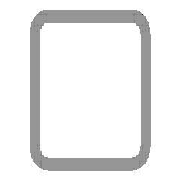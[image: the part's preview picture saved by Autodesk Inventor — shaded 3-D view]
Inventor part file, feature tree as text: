
AUTODESK INVENTOR PART (.ipt)
format: ipt  version: 2021 (Build 250183000, 183)  size: 130,560 bytes
history: native  units: mm (DEFAULTED — no unit token found)
features: other x4, sketch x3, extrude x1, plane x1
ambient origin geometry x8: Origin, YZ Plane, XZ Plane, XY Plane, X Axis, Y Axis, Z Axis, Center Point
bodies: Solid1 (feature_tree)
feature tree (9):
  parser-record x1  (decoder bookkeeping rows leaked as tree rows — omitted from the tree; the rows remain in map.json)
  other  "Driven Length"
  other  "Plano inicial"
  other  "Plano final"
  extrude  "Corpo"  TaperAngle=0.0deg  [1 undecoded]
  sketch  "Esboço"  dims[d11=50.8mm d12=4.7625mm d13=-0.0mm d14=1000.0mm d15=25.4mm d16=25.4mm d17=9.525mm d18=90.0deg d19=1000.0mm]
  sketch  "Sketch3"  dims[d3=1000.0mm d4=0.0mm]
  plane  "Work Plane3"
  sketch  "Sketch4"  dims[d10=50.8mm]
note: 1 required parameter value undecoded (feature->parameter linkage not recoverable at this tier; creation-order binding heuristic only, values carry confidence <= 0.55)
